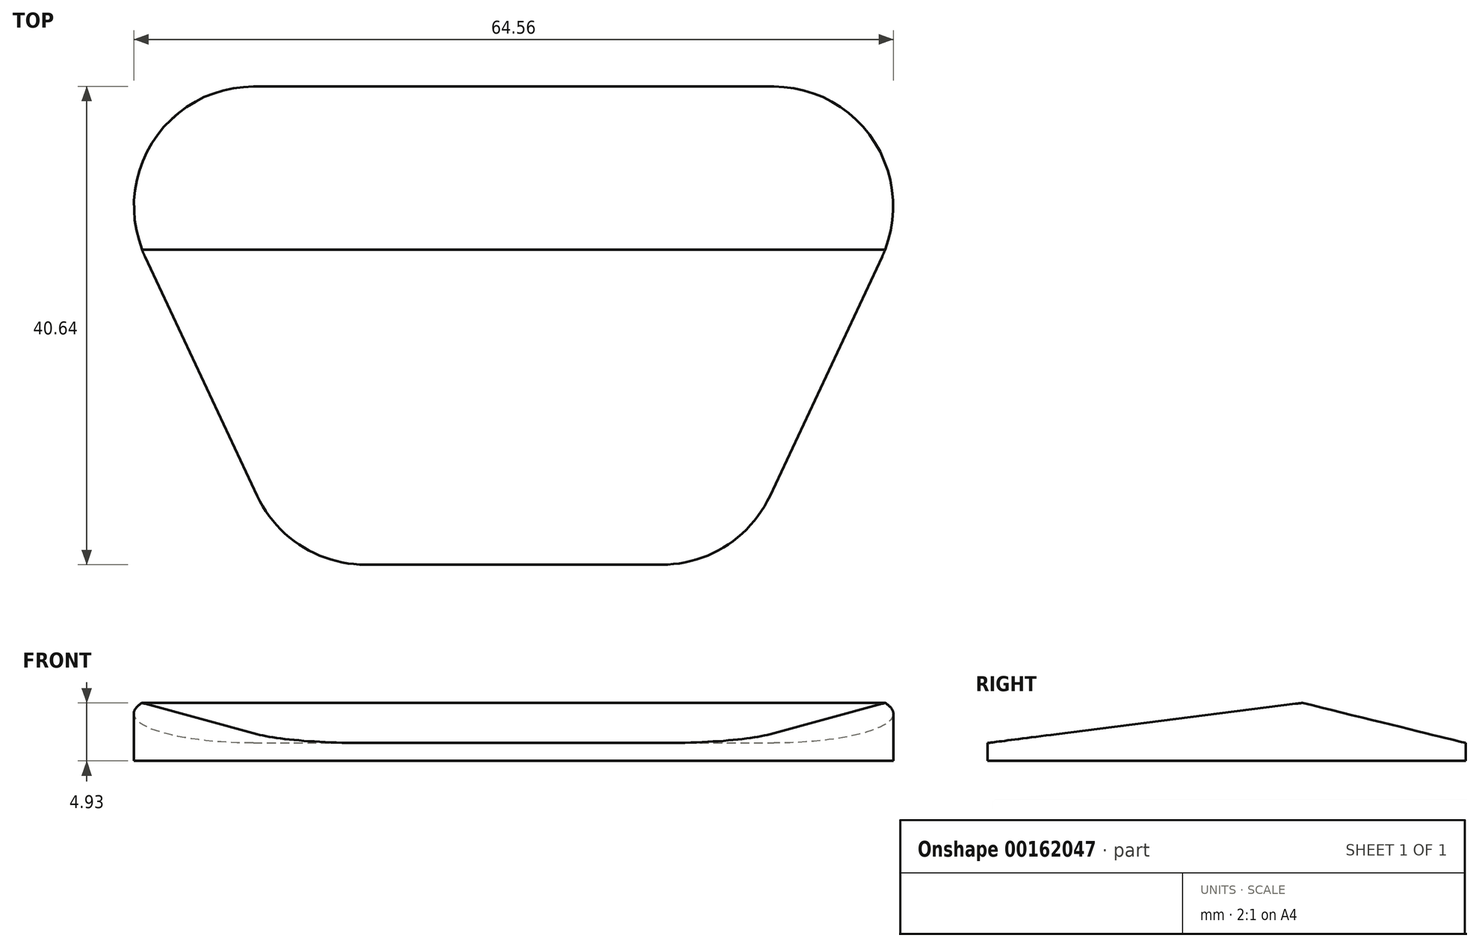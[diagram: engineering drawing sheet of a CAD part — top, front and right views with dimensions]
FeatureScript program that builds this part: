
annotation { "Feature Type Name" : "Feature", "Feature Type Description" : "" }
export const myFeature = defineFeature(function(context is Context, id is Id, definition is map)
    precondition{}
    {
        {
            var Q0;
            Q0=qCreatedBy(makeId("Top.planeOp"),FACE);
            var sketch = newSketch(context, id + "F0", { "sketchPlane" : qUnion([Q0])});
            skLineSegment(sketch, "E0", {"start": v(-19.05, -17.35) * mm, "end": v(19.05, -17.35) * mm});
            skLineSegment(sketch, "E1", {"start": v(19.05, -17.35) * mm, "end": v(38.1, 23.29) * mm});
            skLineSegment(sketch, "E2", {"start": v(38.1, 23.29) * mm, "end": v(-38.1, 23.29) * mm});
            skLineSegment(sketch, "E3", {"start": v(-38.1, 23.29) * mm, "end": v(-19.05, -17.35) * mm});
            skPoint(sketch, "E4", {"position": v(0, 23.29) * mm});
            skPoint(sketch, "E5", {"position": v(0, -17.35) * mm});
            skSolve(sketch);
        }
        {
            var Q0;
            Q0 = qSketchRegion(id + "F0", true);
            extrude(context, id + "F1", {"entities" : qUnion([Q0]), "depth" : 5.08 * mm});
        }
        {
            var Q0;
            Q0=makeQuery(id+"F1.opExtrude","CAP_EDGE",EDGE,{"disambiguationData":[OSD([sQuery(id+"F0.wireOp",EDGE,"E2")])],"isStart":false});
            chamfer(context, id + "F2", {"entities" : qUnion([Q0]), "chamferType" : ChamferType.TWO_OFFSETS, "width1" : 14.48 * mm, "oppositeDirection" : false, "width2" : 3.56 * mm, "tangentPropagation" : true});
        }
        {
            var Q0;
            Q0=makeQuery(id+"F1.opExtrude","CAP_EDGE",EDGE,{"disambiguationData":[OSD([sQuery(id+"F0.wireOp",EDGE,"E0")])],"isStart":false});
            chamfer(context, id + "F3", {"entities" : qUnion([Q0]), "chamferType" : ChamferType.TWO_OFFSETS, "width1" : 27.94 * mm, "oppositeDirection" : false, "width2" : 3.56 * mm, "tangentPropagation" : true});
        }
        {
            var Q0;
            Q0=makeQuery(id+"F1.opExtrude","SWEPT_EDGE",EDGE,{"disambiguationData":[OSD([sQuery(id+"F0.wireOp",EDGE,"E0"),sQuery(id+"F0.wireOp",EDGE,"E1")])]});
            var Q1;
            Q1=makeQuery(id+"F1.opExtrude","SWEPT_EDGE",EDGE,{"disambiguationData":[OSD([sQuery(id+"F0.wireOp",EDGE,"E0"),sQuery(id+"F0.wireOp",EDGE,"E3")])]});
            var Q2;
            Q2=makeQuery(id+"F1.opExtrude","SWEPT_EDGE",EDGE,{"disambiguationData":[OSD([sQuery(id+"F0.wireOp",EDGE,"E1"),sQuery(id+"F0.wireOp",EDGE,"E2")])]});
            var Q3;
            Q3=makeQuery(id+"F1.opExtrude","SWEPT_EDGE",EDGE,{"disambiguationData":[OSD([sQuery(id+"F0.wireOp",EDGE,"E2"),sQuery(id+"F0.wireOp",EDGE,"E3")])]});
            fillet(context, id + "F4", {"entities" : qUnion([Q0, Q1, Q2, Q3]), "radius" : 10.16 * mm, "tangentPropagation" : true, "allowEdgeOverflow" : false});
        }
    });
